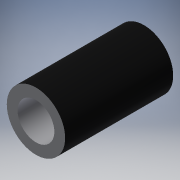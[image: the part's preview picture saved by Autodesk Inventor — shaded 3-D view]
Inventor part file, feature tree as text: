
AUTODESK INVENTOR PART (.ipt)
format: ipt  version: 2016 (Build 200138000, 138)  size: 95,232 bytes
history: native  units: mm
features: extrude x1, sketch x1
ambient origin geometry x8: Origin, YZ Plane, XZ Plane, XY Plane, X Axis, Y Axis, Z Axis, Center Point
bodies: Solid1 (feature_tree)
feature tree (2):
  extrude  "Extrusion1"  Depth=10.0mm
  sketch  "Sketch1"  dims[d0=3.4mm d1=1.0mm d2=10.0mm d3=0.0mm]
